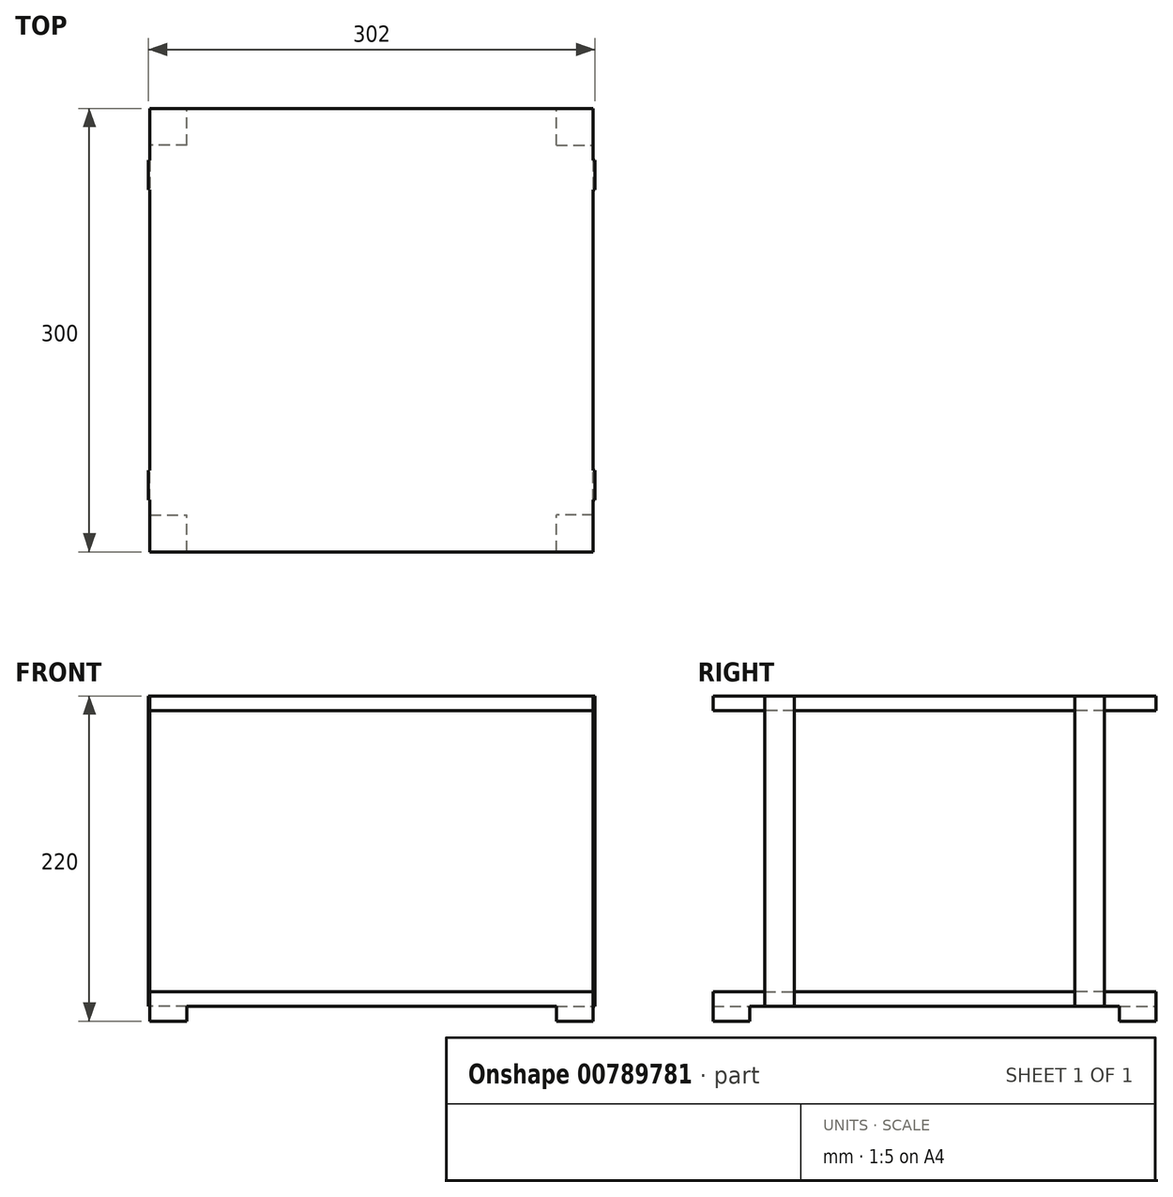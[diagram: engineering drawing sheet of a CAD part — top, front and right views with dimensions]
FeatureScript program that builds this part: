
annotation { "Feature Type Name" : "Feature", "Feature Type Description" : "" }
export const myFeature = defineFeature(function(context is Context, id is Id, definition is map)
    precondition{}
    {
        {
            var Q0;
            Q0=qCreatedBy(makeId("Front.planeOp"),FACE);
            var sketch = newSketch(context, id + "F0", { "sketchPlane" : qUnion([Q0])});
            skLineSegment(sketch, "E0.bottom", {"start": v(-47.07, 39.84) * mm, "end": v(252.93, 39.84) * mm});
            skLineSegment(sketch, "E0.top", {"start": v(-47.07, 29.84) * mm, "end": v(252.93, 29.84) * mm});
            skLineSegment(sketch, "E0.left", {"start": v(-47.07, 39.84) * mm, "end": v(-47.07, 29.84) * mm});
            skLineSegment(sketch, "E0.right", {"start": v(252.93, 39.84) * mm, "end": v(252.93, 29.84) * mm});
            skSolve(sketch);
        }
        {
            var Q0;
            Q0=makeQuery(id+"F0.imprint","IMPRINT",FACE,{"disambiguationData":[TD([[makeQuery(id+"F0.imprint","IMPRINT",EDGE,{"derivedFrom":sQuery(id+"F0.wireOp",EDGE,"E0.bottom")}),-1.0]])]});
            extrude(context, id + "F1", {"entities" : qUnion([Q0]), "depth" : 300 * mm, "offsetDistance" : 25 * mm});
        }
        {
            var Q0;
            Q0=makeQuery(id+"F1.opExtrude","SWEPT_FACE",FACE,{"disambiguationData":[OSD([sQuery(id+"F0.wireOp",EDGE,"E0.top")])]});
            var sketch = newSketch(context, id + "F2", { "sketchPlane" : qUnion([Q0])});
            skPoint(sketch, "E1", {"position": v(-22.07, 275) * mm});
            skLineSegment(sketch, "E2.bottom", {"start": v(-47.07, 300) * mm, "end": v(-22.07, 300) * mm});
            skLineSegment(sketch, "E2.top", {"start": v(-47.07, 275) * mm, "end": v(-22.07, 275) * mm});
            skLineSegment(sketch, "E2.left", {"start": v(-47.07, 300) * mm, "end": v(-47.07, 275) * mm});
            skLineSegment(sketch, "E2.right", {"start": v(-22.07, 300) * mm, "end": v(-22.07, 275) * mm});
            skLineSegment(sketch, "E3.bottom", {"start": v(252.93, 300) * mm, "end": v(227.93, 300) * mm});
            skLineSegment(sketch, "E3.top", {"start": v(252.93, 275) * mm, "end": v(227.93, 275) * mm});
            skLineSegment(sketch, "E3.left", {"start": v(252.93, 300) * mm, "end": v(252.93, 275) * mm});
            skLineSegment(sketch, "E3.right", {"start": v(227.93, 300) * mm, "end": v(227.93, 275) * mm});
            skLineSegment(sketch, "E4.bottom", {"start": v(227.93, 275) * mm, "end": v(-22.07, 275) * mm});
            skLineSegment(sketch, "E4.top", {"start": v(227.93, 25) * mm, "end": v(-22.07, 25) * mm});
            skLineSegment(sketch, "E4.left", {"start": v(227.93, 275) * mm, "end": v(227.93, 25) * mm});
            skLineSegment(sketch, "E4.right", {"start": v(-22.07, 275) * mm, "end": v(-22.07, 25) * mm});
            skLineSegment(sketch, "E5.bottom", {"start": v(227.93, 25) * mm, "end": v(252.93, 25) * mm});
            skLineSegment(sketch, "E5.top", {"start": v(227.93, 0) * mm, "end": v(252.93, 0) * mm});
            skLineSegment(sketch, "E5.left", {"start": v(227.93, 25) * mm, "end": v(227.93, 0) * mm});
            skLineSegment(sketch, "E5.right", {"start": v(252.93, 25) * mm, "end": v(252.93, 0) * mm});
            skLineSegment(sketch, "E6.bottom", {"start": v(-22.07, 25) * mm, "end": v(-47.07, 25) * mm});
            skLineSegment(sketch, "E6.top", {"start": v(-22.07, 0) * mm, "end": v(-47.07, 0) * mm});
            skLineSegment(sketch, "E6.left", {"start": v(-22.07, 25) * mm, "end": v(-22.07, 0) * mm});
            skLineSegment(sketch, "E6.right", {"start": v(-47.07, 25) * mm, "end": v(-47.07, 0) * mm});
            skSolve(sketch);
        }
        {
            var Q0;
            Q0=makeQuery(id+"F2.imprint","IMPRINT",FACE,{"disambiguationData":[TD([[makeQuery(id+"F2.imprint","IMPRINT",EDGE,{"derivedFrom":sQuery(id+"F2.wireOp",EDGE,"E5.bottom")}),-1.0]])]});
            var Q1;
            Q1=makeQuery(id+"F2.imprint","IMPRINT",FACE,{"disambiguationData":[TD([[makeQuery(id+"F2.imprint","IMPRINT",EDGE,{"derivedFrom":sQuery(id+"F2.wireOp",EDGE,"E6.bottom")}),1.0]])]});
            var Q2;
            Q2=makeQuery(id+"F2.imprint","IMPRINT",FACE,{"disambiguationData":[TD([[makeQuery(id+"F2.imprint","IMPRINT",EDGE,{"derivedFrom":sQuery(id+"F2.wireOp",EDGE,"E3.bottom")}),-1.0]])]});
            var Q3;
            Q3=makeQuery(id+"F2.imprint","IMPRINT",FACE,{"disambiguationData":[TD([[makeQuery(id+"F2.imprint","IMPRINT",EDGE,{"derivedFrom":sQuery(id+"F2.wireOp",EDGE,"E2.bottom")}),-1.0]])]});
            extrude(context, id + "F3", {"entities" : qUnion([Q0, Q1, Q2, Q3]), "operationType" : NewBodyOperationType.ADD, "depth" : 10 * mm, "offsetDistance" : 25 * mm});
        }
        {
            var Q0;
            Q0=makeQuery(id+"F3.boolean.opBoolean","MERGE",FACE,{"derivedFrom":[makeQuery(id+"F1.opExtrude","SWEPT_FACE",FACE,{"disambiguationData":[OSD([sQuery(id+"F0.wireOp",EDGE,"E0.right")])]}),makeQuery(id+"F3.opExtrude","SWEPT_FACE",FACE,{"disambiguationData":[OSD([sQuery(id+"F2.wireOp",EDGE,"E3.left")])]}),makeQuery(id+"F3.opExtrude","SWEPT_FACE",FACE,{"disambiguationData":[OSD([sQuery(id+"F2.wireOp",EDGE,"E5.right")])]})]});
            var sketch = newSketch(context, id + "F4", { "sketchPlane" : qUnion([Q0])});
            skLineSegment(sketch, "E7.bottom", {"start": v(-265, 39.84) * mm, "end": v(-245, 39.84) * mm});
            skLineSegment(sketch, "E7.top", {"start": v(-265, 29.84) * mm, "end": v(-245, 29.84) * mm});
            skLineSegment(sketch, "E7.left", {"start": v(-265, 39.84) * mm, "end": v(-265, 29.84) * mm});
            skLineSegment(sketch, "E7.right", {"start": v(-245, 39.84) * mm, "end": v(-245, 29.84) * mm});
            skLineSegment(sketch, "E8.bottom", {"start": v(-55, 39.84) * mm, "end": v(-35, 39.84) * mm});
            skLineSegment(sketch, "E8.top", {"start": v(-55, 29.84) * mm, "end": v(-35, 29.84) * mm});
            skLineSegment(sketch, "E8.left", {"start": v(-55, 39.84) * mm, "end": v(-55, 29.84) * mm});
            skLineSegment(sketch, "E8.right", {"start": v(-35, 39.84) * mm, "end": v(-35, 29.84) * mm});
            skSolve(sketch);
        }
        {
            var Q0;
            Q0=makeQuery(id+"F4.imprint","IMPRINT",FACE,{"disambiguationData":[TD([[makeQuery(id+"F4.imprint","IMPRINT",EDGE,{"derivedFrom":sQuery(id+"F4.wireOp",EDGE,"E8.bottom")}),-1.0]])]});
            var Q1;
            Q1=makeQuery(id+"F4.imprint","IMPRINT",FACE,{"disambiguationData":[TD([[makeQuery(id+"F4.imprint","IMPRINT",EDGE,{"derivedFrom":sQuery(id+"F4.wireOp",EDGE,"E7.bottom")}),-1.0]])]});
            extrude(context, id + "F5", {"entities" : qUnion([Q0, Q1]), "operationType" : NewBodyOperationType.ADD, "depth" : 1 * mm, "offsetDistance" : 25 * mm});
        }
        {
            var Q0;
            Q0=makeQuery(id+"F3.boolean.opBoolean","MERGE",FACE,{"derivedFrom":[makeQuery(id+"F1.opExtrude","SWEPT_FACE",FACE,{"disambiguationData":[OSD([sQuery(id+"F0.wireOp",EDGE,"E0.left")])]}),makeQuery(id+"F3.opExtrude","SWEPT_FACE",FACE,{"disambiguationData":[OSD([sQuery(id+"F2.wireOp",EDGE,"E2.left")])]}),makeQuery(id+"F3.opExtrude","SWEPT_FACE",FACE,{"disambiguationData":[OSD([sQuery(id+"F2.wireOp",EDGE,"E6.right")])]})]});
            var sketch = newSketch(context, id + "F6", { "sketchPlane" : qUnion([Q0])});
            skLineSegment(sketch, "E9.bottom", {"start": v(35, 39.84) * mm, "end": v(55, 39.84) * mm});
            skLineSegment(sketch, "E9.top", {"start": v(35, 29.84) * mm, "end": v(55, 29.84) * mm});
            skLineSegment(sketch, "E9.left", {"start": v(35, 39.84) * mm, "end": v(35, 29.84) * mm});
            skLineSegment(sketch, "E9.right", {"start": v(55, 39.84) * mm, "end": v(55, 29.84) * mm});
            skLineSegment(sketch, "E10.bottom", {"start": v(245, 39.84) * mm, "end": v(265, 39.84) * mm});
            skLineSegment(sketch, "E10.top", {"start": v(245, 29.84) * mm, "end": v(265, 29.84) * mm});
            skLineSegment(sketch, "E10.left", {"start": v(245, 39.84) * mm, "end": v(245, 29.84) * mm});
            skLineSegment(sketch, "E10.right", {"start": v(265, 39.84) * mm, "end": v(265, 29.84) * mm});
            skSolve(sketch);
        }
        {
            var Q0;
            Q0 = qSketchRegion(id + "F6", true);
            extrude(context, id + "F7", {"entities" : qUnion([Q0]), "operationType" : NewBodyOperationType.ADD, "depth" : 1 * mm, "offsetDistance" : 25 * mm});
        }
        {
            var Q0;
            Q0=makeQuery(id+"F7.boolean.opBoolean","MERGE",FACE,{"derivedFrom":[makeQuery(id+"F5.boolean.opBoolean","MERGE",FACE,{"derivedFrom":[makeQuery(id+"F1.opExtrude","SWEPT_FACE",FACE,{"disambiguationData":[OSD([sQuery(id+"F0.wireOp",EDGE,"E0.bottom")])]}),makeQuery(id+"F5.opExtrude","SWEPT_FACE",FACE,{"disambiguationData":[OSD([sQuery(id+"F4.wireOp",EDGE,"E7.bottom")])]}),makeQuery(id+"F5.opExtrude","SWEPT_FACE",FACE,{"disambiguationData":[OSD([sQuery(id+"F4.wireOp",EDGE,"E8.bottom")])]})]}),makeQuery(id+"F7.opExtrude","SWEPT_FACE",FACE,{"disambiguationData":[OSD([sQuery(id+"F6.wireOp",EDGE,"E9.bottom")])]}),makeQuery(id+"F7.opExtrude","SWEPT_FACE",FACE,{"disambiguationData":[OSD([sQuery(id+"F6.wireOp",EDGE,"E10.bottom")])]})]});
            var sketch = newSketch(context, id + "F8", { "sketchPlane" : qUnion([Q0])});
            skLineSegment(sketch, "E11.bottom", {"start": v(253.93, -35) * mm, "end": v(252.93, -35) * mm});
            skLineSegment(sketch, "E11.top", {"start": v(253.93, -55) * mm, "end": v(252.93, -55) * mm});
            skLineSegment(sketch, "E11.left", {"start": v(253.93, -35) * mm, "end": v(253.93, -55) * mm});
            skLineSegment(sketch, "E11.right", {"start": v(252.93, -35) * mm, "end": v(252.93, -55) * mm});
            skLineSegment(sketch, "E12.bottom", {"start": v(253.93, -265) * mm, "end": v(252.93, -265) * mm});
            skLineSegment(sketch, "E12.top", {"start": v(253.93, -245) * mm, "end": v(252.93, -245) * mm});
            skLineSegment(sketch, "E12.left", {"start": v(253.93, -265) * mm, "end": v(253.93, -245) * mm});
            skLineSegment(sketch, "E12.right", {"start": v(252.93, -265) * mm, "end": v(252.93, -245) * mm});
            skLineSegment(sketch, "E13.bottom", {"start": v(-47.07, -265) * mm, "end": v(-48.07, -265) * mm});
            skLineSegment(sketch, "E13.top", {"start": v(-47.07, -245) * mm, "end": v(-48.07, -245) * mm});
            skLineSegment(sketch, "E13.left", {"start": v(-47.07, -265) * mm, "end": v(-47.07, -245) * mm});
            skLineSegment(sketch, "E13.right", {"start": v(-48.07, -265) * mm, "end": v(-48.07, -245) * mm});
            skLineSegment(sketch, "E14.bottom", {"start": v(-48.07, -35) * mm, "end": v(-47.07, -35) * mm});
            skLineSegment(sketch, "E14.top", {"start": v(-48.07, -55) * mm, "end": v(-47.07, -55) * mm});
            skLineSegment(sketch, "E14.left", {"start": v(-48.07, -35) * mm, "end": v(-48.07, -55) * mm});
            skLineSegment(sketch, "E14.right", {"start": v(-47.07, -35) * mm, "end": v(-47.07, -55) * mm});
            skSolve(sketch);
        }
        {
            var Q0;
            Q0 = qSketchRegion(id + "F8", true);
            extrude(context, id + "F9", {"entities" : qUnion([Q0]), "operationType" : NewBodyOperationType.ADD, "depth" : 200 * mm, "offsetDistance" : 25 * mm});
        }
        {
            var Q0;
            Q0=makeQuery(id+"F9.opExtrude","SWEPT_FACE",FACE,{"disambiguationData":[OSD([sQuery(id+"F8.wireOp",EDGE,"E12.right")])]});
            var sketch = newSketch(context, id + "F10", { "sketchPlane" : qUnion([Q0])});
            skLineSegment(sketch, "E15.bottom", {"start": v(0, 239.84) * mm, "end": v(300, 239.84) * mm});
            skLineSegment(sketch, "E15.top", {"start": v(0, 229.84) * mm, "end": v(300, 229.84) * mm});
            skLineSegment(sketch, "E15.left", {"start": v(0, 239.84) * mm, "end": v(0, 229.84) * mm});
            skLineSegment(sketch, "E15.right", {"start": v(300, 239.84) * mm, "end": v(300, 229.84) * mm});
            skSolve(sketch);
        }
        {
            var Q0;
            Q0 = qSketchRegion(id + "F10", true);
            extrude(context, id + "F11", {"entities" : qUnion([Q0]), "operationType" : NewBodyOperationType.ADD, "depth" : 300 * mm, "offsetDistance" : 25 * mm});
        }
    });
